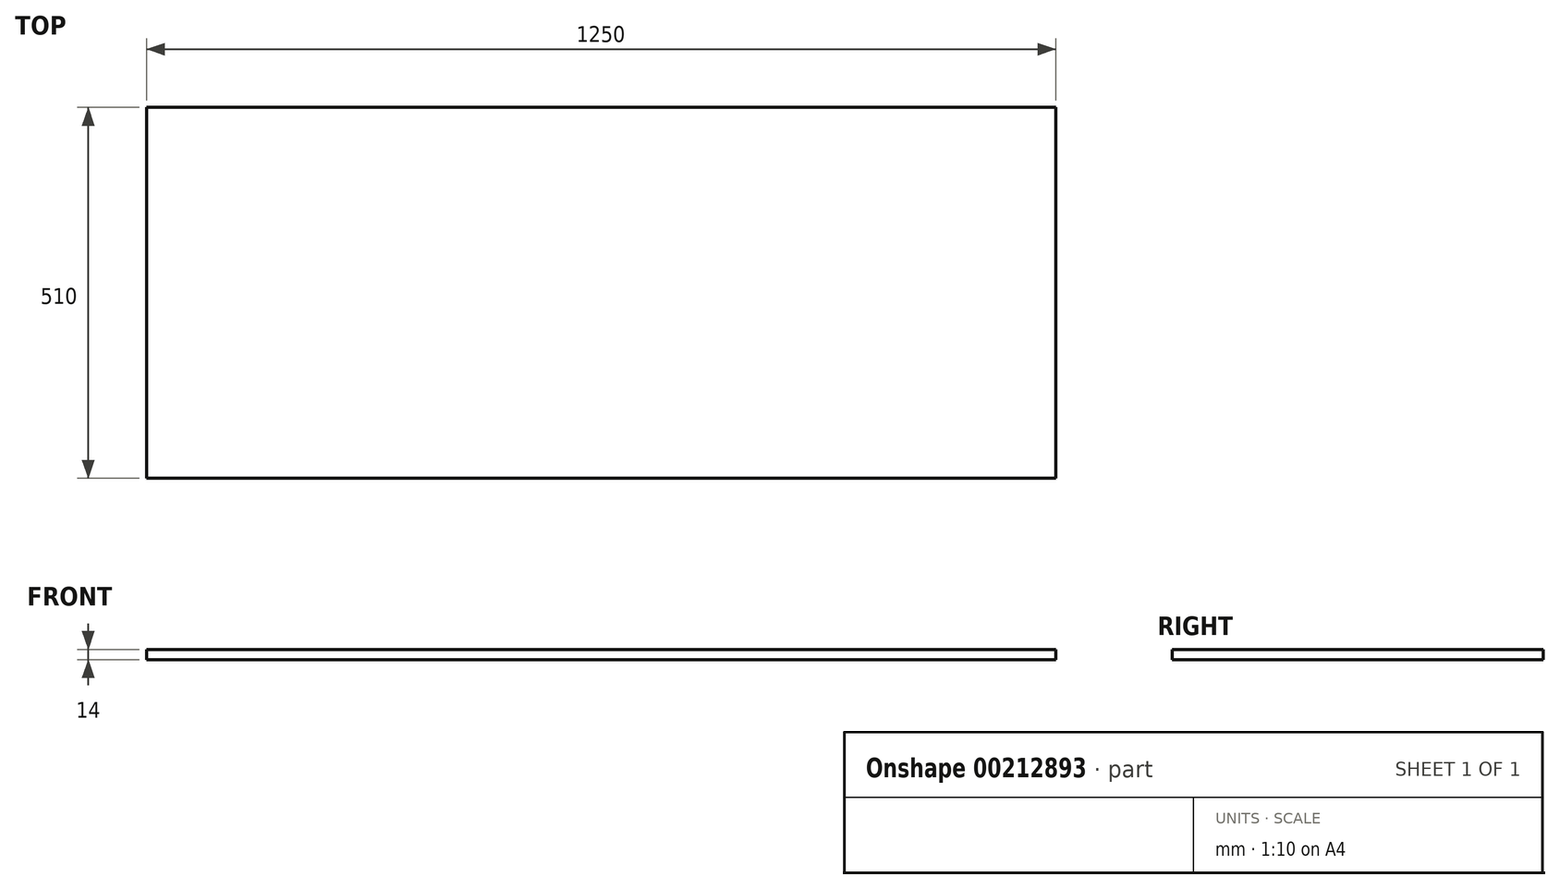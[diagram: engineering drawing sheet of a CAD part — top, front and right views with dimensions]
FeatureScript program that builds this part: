
annotation { "Feature Type Name" : "Feature", "Feature Type Description" : "" }
export const myFeature = defineFeature(function(context is Context, id is Id, definition is map)
    precondition{}
    {
        {
            var Q0;
            Q0=qCreatedBy(makeId("Top.planeOp"),FACE);
            var sketch = newSketch(context, id + "F0", { "sketchPlane" : qUnion([Q0])});
            skLineSegment(sketch, "E0.bottom", {"start": v(0, 0) * mm, "end": v(1250, 0) * mm});
            skLineSegment(sketch, "E0.top", {"start": v(0, -510) * mm, "end": v(1250, -510) * mm});
            skLineSegment(sketch, "E0.left", {"start": v(0, 0) * mm, "end": v(0, -510) * mm});
            skLineSegment(sketch, "E0.right", {"start": v(1250, 0) * mm, "end": v(1250, -510) * mm});
            skSolve(sketch);
        }
        {
            var Q0;
            Q0 = qSketchRegion(id + "F0", true);
            extrude(context, id + "F1", {"entities" : qUnion([Q0]), "depth" : 14 * mm});
        }
    });
